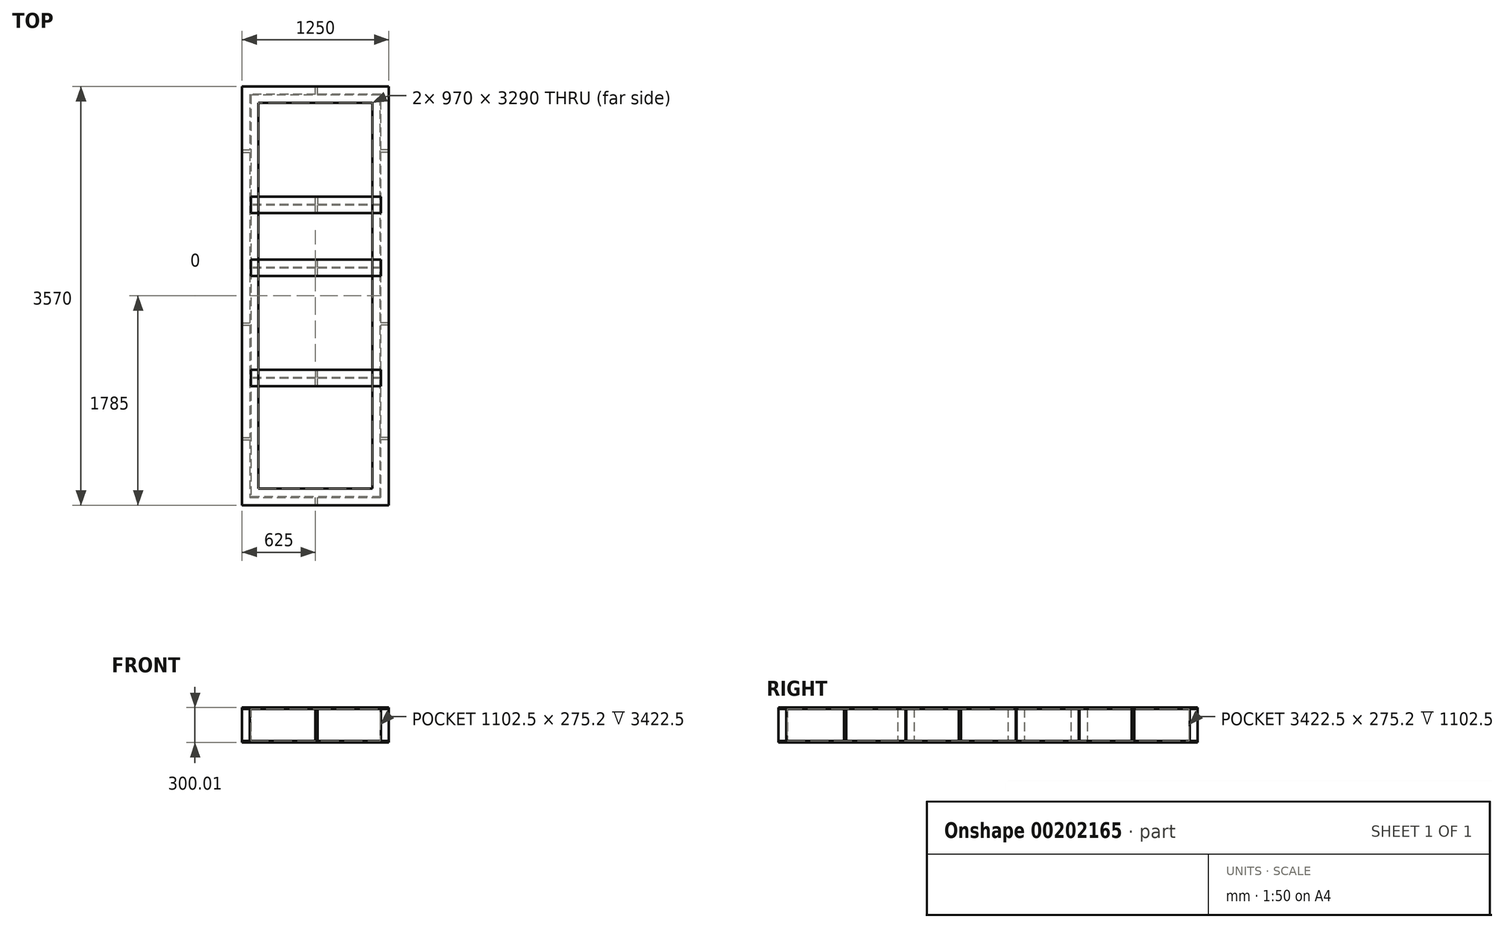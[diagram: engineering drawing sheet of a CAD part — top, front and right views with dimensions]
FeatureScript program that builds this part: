
annotation { "Feature Type Name" : "Feature", "Feature Type Description" : "" }
export const myFeature = defineFeature(function(context is Context, id is Id, definition is map)
    precondition{}
    {
        {
            var Q0;
            Q0=qCreatedBy(makeId("Front.planeOp"),FACE);
            var sketch = newSketch(context, id + "F0", { "sketchPlane" : qUnion([Q0])});
            skLineSegment(sketch, "E0", {"start": v(0, 0) * mm, "end": v(0, -300) * mm, "construction": true});
            skLineSegment(sketch, "E1", {"start": v(0, 0) * mm, "end": v(70, 0) * mm});
            skLineSegment(sketch, "E2", {"start": v(0, 0) * mm, "end": v(-70, 0) * mm});
            skLineSegment(sketch, "E3", {"start": v(-70, 0) * mm, "end": v(-70, -12.4) * mm});
            skLineSegment(sketch, "E4", {"start": v(-70, -12.4) * mm, "end": v(-3.75, -12.4) * mm});
            skLineSegment(sketch, "E5", {"start": v(-3.75, -12.4) * mm, "end": v(-3.75, -287.6) * mm});
            skLineSegment(sketch, "E6", {"start": v(-3.75, -287.6) * mm, "end": v(-70, -287.6) * mm});
            skLineSegment(sketch, "E7", {"start": v(-70, -287.6) * mm, "end": v(-70, -300) * mm});
            skLineSegment(sketch, "E8", {"start": v(-70, -300) * mm, "end": v(70, -300) * mm});
            skLineSegment(sketch, "E9", {"start": v(70, -300) * mm, "end": v(70, -287.6) * mm});
            skLineSegment(sketch, "E10", {"start": v(70, -287.6) * mm, "end": v(3.75, -287.6) * mm});
            skLineSegment(sketch, "E11", {"start": v(3.75, -287.6) * mm, "end": v(3.75, -12.4) * mm});
            skLineSegment(sketch, "E12", {"start": v(3.75, -12.4) * mm, "end": v(70, -12.4) * mm});
            skLineSegment(sketch, "E13", {"start": v(70, -12.4) * mm, "end": v(70, 0) * mm});
            skSolve(sketch);
        }
        {
            var Q0;
            Q0=qCreatedBy(makeId("Right.planeOp"),FACE);
            var sketch = newSketch(context, id + "F1", { "sketchPlane" : qUnion([Q0])});
            skLineSegment(sketch, "E14", {"start": v(0, 0) * mm, "end": v(0, -150) * mm, "construction": true});
            skLineSegment(sketch, "E15", {"start": v(0, -150) * mm, "end": v(-3430, -150) * mm});
            skSolve(sketch);
        }
        {
            var Q0;
            Q0=qCreatedBy(makeId("Front.planeOp"),FACE);
            cPlane(context, id + "F2", {"entities" : qUnion([Q0]), "cplaneType" : CPlaneType.OFFSET, "offset" : 3430 * mm, "width" : 150 * mm, "height" : 150 * mm});
        }
        {
            var Q0;
            Q0=qCreatedBy(id+"F2.planeOp",FACE);
            var sketch = newSketch(context, id + "F3", { "sketchPlane" : qUnion([Q0])});
            skLineSegment(sketch, "E16", {"start": v(0, 0) * mm, "end": v(0, -150) * mm, "construction": true});
            skLineSegment(sketch, "E17", {"start": v(0, -150) * mm, "end": v(1110, -150) * mm});
            skSolve(sketch);
        }
        {
            var Q0;
            Q0=qCreatedBy(makeId("Right.planeOp"),FACE);
            cPlane(context, id + "F4", {"entities" : qUnion([Q0]), "cplaneType" : CPlaneType.OFFSET, "offset" : 1110 * mm, "width" : 150 * mm, "height" : 150 * mm});
        }
        {
            var Q0;
            Q0=qCreatedBy(id+"F4.planeOp",FACE);
            var sketch = newSketch(context, id + "F5", { "sketchPlane" : qUnion([Q0])});
            skLineSegment(sketch, "E18", {"start": v(0, 0) * mm, "end": v(0, -150) * mm, "construction": true});
            skLineSegment(sketch, "E19", {"start": v(0, -150) * mm, "end": v(-3430, -150) * mm});
            skSolve(sketch);
        }
        {
            var Q0;
            Q0=qCreatedBy(makeId("Front.planeOp"),FACE);
            var sketch = newSketch(context, id + "F6", { "sketchPlane" : qUnion([Q0])});
            skLineSegment(sketch, "E20", {"start": v(0, 0) * mm, "end": v(0, -150) * mm, "construction": true});
            skLineSegment(sketch, "E21", {"start": v(0, -150) * mm, "end": v(1110, -150) * mm});
            skSolve(sketch);
        }
        {
            var Q0;
            Q0=makeQuery(id+"F0.imprint","IMPRINT",FACE,{"disambiguationData":[TD([[makeQuery(id+"F0.imprint","IMPRINT",EDGE,{"derivedFrom":sQuery(id+"F0.wireOp",EDGE,"E1")}),-1.0]])]});
            var Q1;
            Q1=qConstructionFilter(qBodyType(qCreatedBy(id+"F0",EDGE),BodyType.WIRE),ConstructionObject.NO);
            var Q2;
            Q2=sQuery(id+"F1.wireOp",EDGE,"E15");
            var Q3;
            Q3=sQuery(id+"F3.wireOp",EDGE,"E17");
            var Q4;
            Q4=sQuery(id+"F5.wireOp",EDGE,"E19");
            var Q5;
            Q5=sQuery(id+"F6.wireOp",EDGE,"E21");
            sweep(context, id + "F7", {"profiles" : qUnion([Q0]), "surfaceProfiles" : qUnion([Q1]), "path" : qUnion([Q2, Q3, Q4, Q5])});
        }
        {
            var Q0;
            Q0=qCreatedBy(makeId("Front.planeOp"),FACE);
            cPlane(context, id + "F8", {"entities" : qUnion([Q0]), "cplaneType" : CPlaneType.OFFSET, "offset" : 940 * mm, "width" : 150 * mm, "height" : 150 * mm});
        }
        {
            var Q0;
            Q0=qCreatedBy(makeId("Front.planeOp"),FACE);
            cPlane(context, id + "F9", {"entities" : qUnion([Q0]), "cplaneType" : CPlaneType.OFFSET, "offset" : 1475 * mm, "width" : 150 * mm, "height" : 150 * mm});
        }
        {
            var Q0;
            Q0=qCreatedBy(makeId("Front.planeOp"),FACE);
            cPlane(context, id + "F10", {"entities" : qUnion([Q0]), "cplaneType" : CPlaneType.OFFSET, "offset" : 2415 * mm, "width" : 150 * mm, "height" : 150 * mm});
        }
        {
            var Q0;
            Q0=qCreatedBy(id+"F8.planeOp",FACE);
            var sketch = newSketch(context, id + "F11", { "sketchPlane" : qUnion([Q0])});
            skLineSegment(sketch, "E22", {"start": v(0, 0) * mm, "end": v(0, -150) * mm, "construction": true});
            skLineSegment(sketch, "E23", {"start": v(0, -150) * mm, "end": v(1110, -150) * mm});
            skSolve(sketch);
        }
        {
            var Q0;
            Q0=makeQuery(id+"F7.opSweep","SWEPT_FACE",FACE,{"disambiguationData":[OSD([sQuery(id+"F0.wireOp",EDGE,"E5"),sQuery(id+"F5.wireOp",EDGE,"E19")])]});
            var sketch = newSketch(context, id + "F12", { "sketchPlane" : qUnion([Q0])});
            skLineSegment(sketch, "E24", {"start": v(0, 0) * mm, "end": v(-940, 0) * mm, "construction": true});
            skLineSegment(sketch, "E25", {"start": v(-940, 0) * mm, "end": v(-940, -150) * mm, "construction": true});
            skLineSegment(sketch, "E26", {"start": v(-939.82, 0) * mm, "end": v(-939.82, -300) * mm, "construction": true});
            skLineSegment(sketch, "E27", {"start": v(-939.82, 0) * mm, "end": v(-869.82, 0) * mm});
            skLineSegment(sketch, "E28", {"start": v(-939.82, 0) * mm, "end": v(-1009.82, 0) * mm});
            skLineSegment(sketch, "E29", {"start": v(-1009.82, 0) * mm, "end": v(-1009.82, -12.4) * mm});
            skLineSegment(sketch, "E30", {"start": v(-1009.82, -12.4) * mm, "end": v(-943.57, -12.4) * mm});
            skLineSegment(sketch, "E31", {"start": v(-943.57, -12.4) * mm, "end": v(-943.57, -287.6) * mm});
            skLineSegment(sketch, "E32", {"start": v(-943.57, -287.6) * mm, "end": v(-1009.82, -287.6) * mm});
            skLineSegment(sketch, "E33", {"start": v(-1009.82, -287.6) * mm, "end": v(-1009.82, -300) * mm});
            skLineSegment(sketch, "E34", {"start": v(-1009.82, -300) * mm, "end": v(-869.82, -300) * mm});
            skLineSegment(sketch, "E35", {"start": v(-869.82, -300) * mm, "end": v(-869.82, -287.6) * mm});
            skLineSegment(sketch, "E36", {"start": v(-869.82, -287.6) * mm, "end": v(-936.07, -287.6) * mm});
            skLineSegment(sketch, "E37", {"start": v(-936.07, -287.6) * mm, "end": v(-936.07, -12.4) * mm});
            skLineSegment(sketch, "E38", {"start": v(-936.07, -12.4) * mm, "end": v(-869.82, -12.4) * mm});
            skLineSegment(sketch, "E39", {"start": v(-869.82, -12.4) * mm, "end": v(-869.82, 0) * mm});
            skSolve(sketch);
        }
        {
            var Q0;
            Q0=qSketchRegion(id+"F12",true);
            var Q1;
            Q1=sQuery(id+"F11.wireOp",EDGE,"E23");
            sweep(context, id + "F13", {"profiles" : qUnion([Q0]), "path" : qUnion([Q1])});
        }
        {
            var Q0;
            Q0=qCreatedBy(id+"F9.planeOp",FACE);
            var sketch = newSketch(context, id + "F14", { "sketchPlane" : qUnion([Q0])});
            skLineSegment(sketch, "E40", {"start": v(0, 0) * mm, "end": v(0, -150) * mm, "construction": true});
            skLineSegment(sketch, "E41", {"start": v(0, -150) * mm, "end": v(1110, -150) * mm});
            skSolve(sketch);
        }
        {
            var Q0;
            Q0=qCreatedBy(id+"F10.planeOp",FACE);
            var sketch = newSketch(context, id + "F15", { "sketchPlane" : qUnion([Q0])});
            skLineSegment(sketch, "E42", {"start": v(0, 0) * mm, "end": v(0, -150) * mm, "construction": true});
            skLineSegment(sketch, "E43", {"start": v(0, -150) * mm, "end": v(1110, -150) * mm});
            skSolve(sketch);
        }
        {
            var Q0;
            Q0=makeQuery(id+"F7.opSweep","SWEPT_FACE",FACE,{"disambiguationData":[OSD([sQuery(id+"F0.wireOp",EDGE,"E5"),sQuery(id+"F5.wireOp",EDGE,"E19")])]});
            var sketch = newSketch(context, id + "F16", { "sketchPlane" : qUnion([Q0])});
            skLineSegment(sketch, "E44", {"start": v(0, 0) * mm, "end": v(-2415, 0) * mm, "construction": true});
            skLineSegment(sketch, "E45", {"start": v(-2415, 0) * mm, "end": v(-2415, -150) * mm, "construction": true});
            skLineSegment(sketch, "E46", {"start": v(-2415.04, 0) * mm, "end": v(-2415.04, -300) * mm, "construction": true});
            skLineSegment(sketch, "E47", {"start": v(-2415.04, 0) * mm, "end": v(-2345.04, 0) * mm});
            skLineSegment(sketch, "E48", {"start": v(-2415.04, 0) * mm, "end": v(-2485.04, 0) * mm});
            skLineSegment(sketch, "E49", {"start": v(-2485.04, 0) * mm, "end": v(-2485.04, -12.4) * mm});
            skLineSegment(sketch, "E50", {"start": v(-2485.04, -12.4) * mm, "end": v(-2418.79, -12.4) * mm});
            skLineSegment(sketch, "E51", {"start": v(-2418.79, -12.4) * mm, "end": v(-2418.79, -287.6) * mm});
            skLineSegment(sketch, "E52", {"start": v(-2418.79, -287.6) * mm, "end": v(-2485.04, -287.6) * mm});
            skLineSegment(sketch, "E53", {"start": v(-2485.04, -287.6) * mm, "end": v(-2485.04, -300) * mm});
            skLineSegment(sketch, "E54", {"start": v(-2485.04, -300) * mm, "end": v(-2345.04, -300) * mm});
            skLineSegment(sketch, "E55", {"start": v(-2345.04, -300) * mm, "end": v(-2345.04, -287.6) * mm});
            skLineSegment(sketch, "E56", {"start": v(-2345.04, -287.6) * mm, "end": v(-2411.29, -287.6) * mm});
            skLineSegment(sketch, "E57", {"start": v(-2411.29, -287.6) * mm, "end": v(-2411.29, -12.4) * mm});
            skLineSegment(sketch, "E58", {"start": v(-2411.29, -12.4) * mm, "end": v(-2345.04, -12.4) * mm});
            skLineSegment(sketch, "E59", {"start": v(-2345.04, -12.4) * mm, "end": v(-2345.04, 0) * mm});
            skSolve(sketch);
        }
        {
            var Q0;
            {var subQ2=sQuery(id+"F16.wireOp",EDGE,"E56");Q0=makeQuery(id+"F16.imprint","IMPRINT",FACE,{"disambiguationData":[TD([[makeQuery(id+"F16.imprint","IMPRINT",EDGE,{"derivedFrom":subQ2}),-1.0]])]});}
            var sketch = newSketch(context, id + "F17", { "sketchPlane" : qUnion([Q0])});
            skLineSegment(sketch, "E60", {"start": v(0, 0) * mm, "end": v(-1475, 0) * mm, "construction": true});
            skLineSegment(sketch, "E61", {"start": v(-1475, 0) * mm, "end": v(-1475, -150) * mm, "construction": true});
            skLineSegment(sketch, "E62", {"start": v(-1474.96, 0) * mm, "end": v(-1474.96, -300) * mm, "construction": true});
            skLineSegment(sketch, "E63", {"start": v(-1474.96, 0) * mm, "end": v(-1404.96, 0) * mm});
            skLineSegment(sketch, "E64", {"start": v(-1474.96, 0) * mm, "end": v(-1544.96, 0) * mm});
            skLineSegment(sketch, "E65", {"start": v(-1544.96, 0) * mm, "end": v(-1544.96, -12.4) * mm});
            skLineSegment(sketch, "E66", {"start": v(-1544.96, -12.4) * mm, "end": v(-1478.7, -12.4) * mm});
            skLineSegment(sketch, "E67", {"start": v(-1478.7, -12.4) * mm, "end": v(-1478.7, -287.6) * mm});
            skLineSegment(sketch, "E68", {"start": v(-1478.7, -287.6) * mm, "end": v(-1544.96, -287.6) * mm});
            skLineSegment(sketch, "E69", {"start": v(-1544.96, -287.6) * mm, "end": v(-1544.96, -300) * mm});
            skLineSegment(sketch, "E70", {"start": v(-1544.96, -300) * mm, "end": v(-1404.96, -300) * mm});
            skLineSegment(sketch, "E71", {"start": v(-1404.96, -300) * mm, "end": v(-1404.96, -287.6) * mm});
            skLineSegment(sketch, "E72", {"start": v(-1404.96, -287.6) * mm, "end": v(-1471.2, -287.6) * mm});
            skLineSegment(sketch, "E73", {"start": v(-1471.2, -287.6) * mm, "end": v(-1471.2, -12.4) * mm});
            skLineSegment(sketch, "E74", {"start": v(-1471.2, -12.4) * mm, "end": v(-1404.96, -12.4) * mm});
            skLineSegment(sketch, "E75", {"start": v(-1404.96, -12.4) * mm, "end": v(-1404.96, 0) * mm});
            skSolve(sketch);
        }
        {
            var Q0;
            Q0=qSketchRegion(id+"F17",true);
            var Q1;
            Q1=sQuery(id+"F14.wireOp",EDGE,"E41");
            sweep(context, id + "F18", {"profiles" : qUnion([Q0]), "path" : qUnion([Q1])});
        }
        {
            var Q0;
            Q0=qSketchRegion(id+"F16",true);
            var Q1;
            Q1=sQuery(id+"F15.wireOp",EDGE,"E43");
            sweep(context, id + "F19", {"profiles" : qUnion([Q0]), "path" : qUnion([Q1])});
        }
        {
            var Q0;
            Q0=qCreatedBy(id+"F10.planeOp",FACE);
            cPlane(context, id + "F20", {"entities" : qUnion([Q0]), "cplaneType" : CPlaneType.OFFSET, "offset" : 470 * mm, "oppositeDirection" : true, "width" : 150 * mm, "height" : 150 * mm});
        }
        {
            var Q0;
            Q0=qCreatedBy(id+"F20.planeOp",FACE);
            var sketch = newSketch(context, id + "F21", { "sketchPlane" : qUnion([Q0])});
            skLineSegment(sketch, "E76.0", {"start": v(-70, -12.4) * mm, "end": v(0, -12.4) * mm});
            skLineSegment(sketch, "E77", {"start": v(-70, -12.4) * mm, "end": v(-70, -287.6) * mm});
            skLineSegment(sketch, "E78", {"start": v(-70, -287.6) * mm, "end": v(0, -287.6) * mm});
            skLineSegment(sketch, "E79", {"start": v(0, -287.6) * mm, "end": v(0, -12.4) * mm});
            skPoint(sketch, "E80.orphan", {"position": v(1180, -12.4) * mm});
            skSolve(sketch);
        }
        {
            var Q0;
            Q0=qSketchRegion(id+"F21",true);
            extrude(context, id + "F22", {"entities" : qUnion([Q0]), "operationType" : NewBodyOperationType.ADD, "depth" : 20 * mm});
        }
        {
            var Q0;
            Q0=makeQuery(id+"Fla3xzbbfieMJ2c_5.opBoolean","MERGE",FACE,{"derivedFrom":[makeQuery(id+"F7.opSweep","SWEPT_FACE",FACE,{"disambiguationData":[OSD([sQuery(id+"F0.wireOp",EDGE,"E5"),sQuery(id+"F5.wireOp",EDGE,"E19")])]}),makeQuery(id+"F13.opSweep","CAP_FACE",FACE,{"disambiguationData":[OSD([sQuery(id+"F11.wireOp",VERTEX,"E23.end"),sQuery(id+"F12.wireOp",EDGE,"E27"),sQuery(id+"F12.wireOp",EDGE,"E28"),sQuery(id+"F12.wireOp",EDGE,"E29"),sQuery(id+"F12.wireOp",EDGE,"E30"),sQuery(id+"F12.wireOp",EDGE,"E31"),sQuery(id+"F12.wireOp",EDGE,"E32"),sQuery(id+"F12.wireOp",EDGE,"E33"),sQuery(id+"F12.wireOp",EDGE,"E34"),sQuery(id+"F12.wireOp",EDGE,"E35"),sQuery(id+"F12.wireOp",EDGE,"E36"),sQuery(id+"F12.wireOp",EDGE,"E37"),sQuery(id+"F12.wireOp",EDGE,"E38"),sQuery(id+"F12.wireOp",EDGE,"E39")])],"isStart":true}),makeQuery(id+"F18.opSweep","CAP_FACE",FACE,{"disambiguationData":[OSD([sQuery(id+"F14.wireOp",VERTEX,"E41.end"),sQuery(id+"F17.wireOp",EDGE,"E63"),sQuery(id+"F17.wireOp",EDGE,"E64"),sQuery(id+"F17.wireOp",EDGE,"E65"),sQuery(id+"F17.wireOp",EDGE,"E66"),sQuery(id+"F17.wireOp",EDGE,"E67"),sQuery(id+"F17.wireOp",EDGE,"E68"),sQuery(id+"F17.wireOp",EDGE,"E69"),sQuery(id+"F17.wireOp",EDGE,"E70"),sQuery(id+"F17.wireOp",EDGE,"E71"),sQuery(id+"F17.wireOp",EDGE,"E72"),sQuery(id+"F17.wireOp",EDGE,"E73"),sQuery(id+"F17.wireOp",EDGE,"E74"),sQuery(id+"F17.wireOp",EDGE,"E75")])],"isStart":true}),makeQuery(id+"F19.opSweep","CAP_FACE",FACE,{"disambiguationData":[OSD([sQuery(id+"F15.wireOp",VERTEX,"E43.end"),sQuery(id+"F16.wireOp",EDGE,"E47"),sQuery(id+"F16.wireOp",EDGE,"E48"),sQuery(id+"F16.wireOp",EDGE,"E49"),sQuery(id+"F16.wireOp",EDGE,"E50"),sQuery(id+"F16.wireOp",EDGE,"E51"),sQuery(id+"F16.wireOp",EDGE,"E52"),sQuery(id+"F16.wireOp",EDGE,"E53"),sQuery(id+"F16.wireOp",EDGE,"E54"),sQuery(id+"F16.wireOp",EDGE,"E55"),sQuery(id+"F16.wireOp",EDGE,"E56"),sQuery(id+"F16.wireOp",EDGE,"E57"),sQuery(id+"F16.wireOp",EDGE,"E58"),sQuery(id+"F16.wireOp",EDGE,"E59")])],"isStart":true})]});
            var sketch = newSketch(context, id + "F23", { "sketchPlane" : qUnion([Q0])});
            skLineSegment(sketch, "E81.0", {"start": v(-1945, -12.4) * mm, "end": v(-1945, -287.6) * mm});
            skLineSegment(sketch, "E82.0", {"start": v(-1965, -12.4) * mm, "end": v(-1965, -287.6) * mm});
            skLineSegment(sketch, "E83", {"start": v(-1965, -12.4) * mm, "end": v(-1945, -12.4) * mm});
            skLineSegment(sketch, "E84", {"start": v(-1965, -287.6) * mm, "end": v(-1945, -287.6) * mm});
            skSolve(sketch);
        }
        {
            var Q0;
            Q0=qSketchRegion(id+"F23",true);
            extrude(context, id + "F24", {"entities" : qUnion([Q0]), "operationType" : NewBodyOperationType.ADD, "depth" : 66 * mm});
        }
        {
            var Q0;
            Q0=qCreatedBy(id+"F10.planeOp",FACE);
            cPlane(context, id + "F25", {"entities" : qUnion([Q0]), "cplaneType" : CPlaneType.OFFSET, "offset" : 507.5 * mm, "width" : 150 * mm, "height" : 150 * mm});
        }
        {
            var Q0;
            Q0=qCreatedBy(makeId("Front.planeOp"),FACE);
            cPlane(context, id + "F26", {"entities" : qUnion([Q0]), "cplaneType" : CPlaneType.OFFSET, "offset" : 470 * mm, "width" : 150 * mm, "height" : 150 * mm});
        }
        {
            var Q0;
            Q0=qCreatedBy(id+"F26.planeOp",FACE);
            var sketch = newSketch(context, id + "F27", { "sketchPlane" : qUnion([Q0])});
            skLineSegment(sketch, "E85.0", {"start": v(-70, -12.4) * mm, "end": v(0, -12.4) * mm});
            skLineSegment(sketch, "E86", {"start": v(-70, -12.4) * mm, "end": v(-70, -287.6) * mm});
            skLineSegment(sketch, "E87", {"start": v(-70, -287.6) * mm, "end": v(0, -287.6) * mm});
            skLineSegment(sketch, "E88", {"start": v(0, -287.6) * mm, "end": v(0, -12.4) * mm});
            skPoint(sketch, "E89.orphan", {"position": v(1180, -12.4) * mm});
            skSolve(sketch);
        }
        {
            var Q0;
            Q0=qSketchRegion(id+"F27",true);
            extrude(context, id + "F28", {"entities" : qUnion([Q0]), "operationType" : NewBodyOperationType.ADD, "depth" : 20 * mm});
        }
        {
            var Q0;
            Q0=qCreatedBy(id+"F25.planeOp",FACE);
            var sketch = newSketch(context, id + "F29", { "sketchPlane" : qUnion([Q0])});
            skLineSegment(sketch, "E90.0", {"start": v(-70, -12.4) * mm, "end": v(0, -12.4) * mm});
            skLineSegment(sketch, "E91", {"start": v(-70, -12.4) * mm, "end": v(-70, -287.6) * mm});
            skLineSegment(sketch, "E92", {"start": v(-70, -287.6) * mm, "end": v(0, -287.6) * mm});
            skLineSegment(sketch, "E93", {"start": v(0, -287.6) * mm, "end": v(0, -12.4) * mm});
            skPoint(sketch, "E94.orphan", {"position": v(1180, -12.4) * mm});
            skSolve(sketch);
        }
        {
            var Q0;
            Q0=qSketchRegion(id+"F29",true);
            extrude(context, id + "F30", {"entities" : qUnion([Q0]), "operationType" : NewBodyOperationType.ADD, "depth" : 20 * mm});
        }
        {
            var Q0;
            {var subQ1=sQuery(id+"F0.wireOp",EDGE,"E5");Q0=makeQuery(id+"F24.boolean.opBoolean","SPLIT",FACE,{"disambiguationData":[TD([makeQuery(id+"F24.opExtrude","SWEPT_FACE",FACE,{"disambiguationData":[OSD([sQuery(id+"F23.wireOp",EDGE,"E81.0")])]})])],"derivedFrom":makeQuery(id+"Fla3xzbbfieMJ2c_5.opBoolean","MERGE",FACE,{"derivedFrom":[makeQuery(id+"F7.opSweep","SWEPT_FACE",FACE,{"disambiguationData":[OSD([subQ1,sQuery(id+"F5.wireOp",EDGE,"E19")])]}),makeQuery(id+"F13.opSweep","CAP_FACE",FACE,{"disambiguationData":[OSD([sQuery(id+"F11.wireOp",VERTEX,"E23.end"),sQuery(id+"F12.wireOp",EDGE,"E27"),sQuery(id+"F12.wireOp",EDGE,"E28"),sQuery(id+"F12.wireOp",EDGE,"E29"),sQuery(id+"F12.wireOp",EDGE,"E30"),sQuery(id+"F12.wireOp",EDGE,"E31"),sQuery(id+"F12.wireOp",EDGE,"E32"),sQuery(id+"F12.wireOp",EDGE,"E33"),sQuery(id+"F12.wireOp",EDGE,"E34"),sQuery(id+"F12.wireOp",EDGE,"E35"),sQuery(id+"F12.wireOp",EDGE,"E36"),sQuery(id+"F12.wireOp",EDGE,"E37"),sQuery(id+"F12.wireOp",EDGE,"E38"),sQuery(id+"F12.wireOp",EDGE,"E39")])],"isStart":true}),makeQuery(id+"F18.opSweep","CAP_FACE",FACE,{"disambiguationData":[OSD([sQuery(id+"F14.wireOp",VERTEX,"E41.end"),sQuery(id+"F17.wireOp",EDGE,"E63"),sQuery(id+"F17.wireOp",EDGE,"E64"),sQuery(id+"F17.wireOp",EDGE,"E65"),sQuery(id+"F17.wireOp",EDGE,"E66"),sQuery(id+"F17.wireOp",EDGE,"E67"),sQuery(id+"F17.wireOp",EDGE,"E68"),sQuery(id+"F17.wireOp",EDGE,"E69"),sQuery(id+"F17.wireOp",EDGE,"E70"),sQuery(id+"F17.wireOp",EDGE,"E71"),sQuery(id+"F17.wireOp",EDGE,"E72"),sQuery(id+"F17.wireOp",EDGE,"E73"),sQuery(id+"F17.wireOp",EDGE,"E74"),sQuery(id+"F17.wireOp",EDGE,"E75")])],"isStart":true}),makeQuery(id+"F19.opSweep","CAP_FACE",FACE,{"disambiguationData":[OSD([sQuery(id+"F15.wireOp",VERTEX,"E43.end"),sQuery(id+"F16.wireOp",EDGE,"E47"),sQuery(id+"F16.wireOp",EDGE,"E48"),sQuery(id+"F16.wireOp",EDGE,"E49"),sQuery(id+"F16.wireOp",EDGE,"E50"),sQuery(id+"F16.wireOp",EDGE,"E51"),sQuery(id+"F16.wireOp",EDGE,"E52"),sQuery(id+"F16.wireOp",EDGE,"E53"),sQuery(id+"F16.wireOp",EDGE,"E54"),sQuery(id+"F16.wireOp",EDGE,"E55"),sQuery(id+"F16.wireOp",EDGE,"E56"),sQuery(id+"F16.wireOp",EDGE,"E57"),sQuery(id+"F16.wireOp",EDGE,"E58"),sQuery(id+"F16.wireOp",EDGE,"E59")])],"isStart":true})]})});}
            var sketch = newSketch(context, id + "F31", { "sketchPlane" : qUnion([Q0])});
            skLineSegment(sketch, "E95.0", {"start": v(-470, -12.4) * mm, "end": v(-470, -287.6) * mm});
            skLineSegment(sketch, "E96.0", {"start": v(-490, -12.4) * mm, "end": v(-490, -287.6) * mm});
            skLineSegment(sketch, "E97.0", {"start": v(-2922.5, -12.4) * mm, "end": v(-2922.5, -287.6) * mm});
            skLineSegment(sketch, "E98.0", {"start": v(-2942.5, -12.4) * mm, "end": v(-2942.5, -287.6) * mm});
            skLineSegment(sketch, "E99", {"start": v(-2942.5, -12.4) * mm, "end": v(-2922.5, -12.4) * mm});
            skLineSegment(sketch, "E100", {"start": v(-2942.5, -287.6) * mm, "end": v(-2922.5, -287.6) * mm});
            skLineSegment(sketch, "E101", {"start": v(-490, -12.4) * mm, "end": v(-470, -12.4) * mm});
            skLineSegment(sketch, "E102", {"start": v(-490, -287.6) * mm, "end": v(-470, -287.6) * mm});
            skSolve(sketch);
        }
        {
            var Q0;
            Q0=qSketchRegion(id+"F31",true);
            extrude(context, id + "F32", {"entities" : qUnion([Q0]), "operationType" : NewBodyOperationType.ADD, "depth" : 66 * mm});
        }
        {
            var Q0;
            Q0=qCreatedBy(makeId("Right.planeOp"),FACE);
            cPlane(context, id + "F33", {"entities" : qUnion([Q0]), "cplaneType" : CPlaneType.OFFSET, "offset" : 555 * mm, "width" : 150 * mm, "height" : 150 * mm});
        }
        {
            var Q0;
            Q0=qCreatedBy(id+"F33.planeOp",FACE);
            var sketch = newSketch(context, id + "F34", { "sketchPlane" : qUnion([Q0])});
            skLineSegment(sketch, "E103.0", {"start": v(0, -12.4) * mm, "end": v(70, -12.4) * mm});
            skLineSegment(sketch, "E104", {"start": v(70, -12.4) * mm, "end": v(70, -287.6) * mm});
            skLineSegment(sketch, "E105", {"start": v(70, -287.6) * mm, "end": v(0, -287.6) * mm});
            skLineSegment(sketch, "E106", {"start": v(0, -287.6) * mm, "end": v(0, -12.4) * mm});
            skPoint(sketch, "E107.orphan", {"position": v(-3500, -12.4) * mm});
            skSolve(sketch);
        }
        {
            var Q0;
            Q0=qSketchRegion(id+"F34",true);
            extrude(context, id + "F35", {"entities" : qUnion([Q0]), "operationType" : NewBodyOperationType.ADD, "depth" : 20 * mm});
        }
        {
            var Q0;
            Q0=makeQuery(id+"F7.opSweep","SWEPT_FACE",FACE,{"disambiguationData":[OSD([sQuery(id+"F0.wireOp",EDGE,"E5"),sQuery(id+"F3.wireOp",EDGE,"E17")])]});
            var sketch = newSketch(context, id + "F36", { "sketchPlane" : qUnion([Q0])});
            skLineSegment(sketch, "E108.0", {"start": v(575, -12.4) * mm, "end": v(575, -287.6) * mm});
            skLineSegment(sketch, "E109.0", {"start": v(555, -12.4) * mm, "end": v(555, -287.6) * mm});
            skLineSegment(sketch, "E110", {"start": v(555, -12.4) * mm, "end": v(575, -12.4) * mm});
            skLineSegment(sketch, "E111", {"start": v(555, -287.6) * mm, "end": v(575, -287.6) * mm});
            skSolve(sketch);
        }
        {
            var Q0;
            Q0=qSketchRegion(id+"F36",true);
            extrude(context, id + "F37", {"entities" : qUnion([Q0]), "operationType" : NewBodyOperationType.ADD, "depth" : 66 * mm});
        }
        {
            var Q0;
            Q0=makeQuery(id+"F19.opSweep","SWEPT_FACE",FACE,{"disambiguationData":[OSD([sQuery(id+"F15.wireOp",EDGE,"E43"),sQuery(id+"F16.wireOp",EDGE,"E51")])]});
            var sketch = newSketch(context, id + "F38", { "sketchPlane" : qUnion([Q0])});
            skLineSegment(sketch, "E112.0", {"start": v(555, -12.4) * mm, "end": v(555, -287.6) * mm});
            skLineSegment(sketch, "E113.0", {"start": v(575, -12.4) * mm, "end": v(575, -287.6) * mm});
            skLineSegment(sketch, "E114", {"start": v(555, -12.4) * mm, "end": v(575, -12.4) * mm});
            skLineSegment(sketch, "E115", {"start": v(555, -287.6) * mm, "end": v(575, -287.6) * mm});
            skSolve(sketch);
        }
        {
            var Q0;
            Q0=qSketchRegion(id+"F38",true);
            extrude(context, id + "F39", {"entities" : qUnion([Q0]), "operationType" : NewBodyOperationType.ADD, "depth" : 66 * mm});
        }
        {
            var Q0;
            Q0=makeQuery(id+"F19.opSweep","SWEPT_FACE",FACE,{"disambiguationData":[OSD([sQuery(id+"F15.wireOp",EDGE,"E43"),sQuery(id+"F16.wireOp",EDGE,"E57")])]});
            var sketch = newSketch(context, id + "F40", { "sketchPlane" : qUnion([Q0])});
            skLineSegment(sketch, "E116.0", {"start": v(-555, -12.4) * mm, "end": v(-555, -287.6) * mm});
            skLineSegment(sketch, "E117.0", {"start": v(-575, -12.4) * mm, "end": v(-575, -287.6) * mm});
            skLineSegment(sketch, "E118", {"start": v(-555, -12.4) * mm, "end": v(-575, -12.4) * mm});
            skLineSegment(sketch, "E119", {"start": v(-555, -287.6) * mm, "end": v(-575, -287.6) * mm});
            skSolve(sketch);
        }
        {
            var Q0;
            Q0=qSketchRegion(id+"F40",true);
            extrude(context, id + "F41", {"entities" : qUnion([Q0]), "operationType" : NewBodyOperationType.ADD, "depth" : 66 * mm});
        }
        {
            var Q0;
            Q0=makeQuery(id+"F18.opSweep","SWEPT_FACE",FACE,{"disambiguationData":[OSD([sQuery(id+"F14.wireOp",EDGE,"E41"),sQuery(id+"F17.wireOp",EDGE,"E67")])]});
            var sketch = newSketch(context, id + "F42", { "sketchPlane" : qUnion([Q0])});
            skLineSegment(sketch, "E120.0", {"start": v(555, -12.4) * mm, "end": v(555, -287.6) * mm});
            skLineSegment(sketch, "E121.0", {"start": v(575, -12.4) * mm, "end": v(575, -287.6) * mm});
            skLineSegment(sketch, "E122", {"start": v(555, -12.4) * mm, "end": v(575, -12.4) * mm});
            skLineSegment(sketch, "E123", {"start": v(555, -287.6) * mm, "end": v(575, -287.6) * mm});
            skSolve(sketch);
        }
        {
            var Q0;
            Q0=qSketchRegion(id+"F42",true);
            extrude(context, id + "F43", {"entities" : qUnion([Q0]), "operationType" : NewBodyOperationType.ADD, "depth" : 66 * mm});
        }
        {
            var Q0;
            Q0=makeQuery(id+"F18.opSweep","SWEPT_FACE",FACE,{"disambiguationData":[OSD([sQuery(id+"F14.wireOp",EDGE,"E41"),sQuery(id+"F17.wireOp",EDGE,"E73")])]});
            var sketch = newSketch(context, id + "F44", { "sketchPlane" : qUnion([Q0])});
            skLineSegment(sketch, "E124.0", {"start": v(-575, -12.4) * mm, "end": v(-575, -287.6) * mm});
            skLineSegment(sketch, "E125.0", {"start": v(-555, -12.4) * mm, "end": v(-555, -287.6) * mm});
            skLineSegment(sketch, "E126", {"start": v(-575, -12.4) * mm, "end": v(-555, -12.4) * mm});
            skLineSegment(sketch, "E127", {"start": v(-575, -287.6) * mm, "end": v(-555, -287.6) * mm});
            skSolve(sketch);
        }
        {
            var Q0;
            Q0=qSketchRegion(id+"F44",true);
            extrude(context, id + "F45", {"entities" : qUnion([Q0]), "operationType" : NewBodyOperationType.ADD, "depth" : 66 * mm});
        }
        {
            var Q0;
            Q0=makeQuery(id+"F13.opSweep","SWEPT_FACE",FACE,{"disambiguationData":[OSD([sQuery(id+"F11.wireOp",EDGE,"E23"),sQuery(id+"F12.wireOp",EDGE,"E37")])]});
            var sketch = newSketch(context, id + "F46", { "sketchPlane" : qUnion([Q0])});
            skLineSegment(sketch, "E128.0", {"start": v(-575, -12.4) * mm, "end": v(-575, -287.6) * mm});
            skLineSegment(sketch, "E129.0", {"start": v(-555, -12.4) * mm, "end": v(-555, -287.6) * mm});
            skLineSegment(sketch, "E130", {"start": v(-575, -12.4) * mm, "end": v(-555, -12.4) * mm});
            skLineSegment(sketch, "E131", {"start": v(-575, -287.6) * mm, "end": v(-555, -287.6) * mm});
            skSolve(sketch);
        }
        {
            var Q0;
            Q0=qSketchRegion(id+"F46",true);
            extrude(context, id + "F47", {"entities" : qUnion([Q0]), "operationType" : NewBodyOperationType.ADD, "depth" : 66 * mm});
        }
        {
            var Q0;
            Q0=makeQuery(id+"F13.opSweep","SWEPT_FACE",FACE,{"disambiguationData":[OSD([sQuery(id+"F11.wireOp",EDGE,"E23"),sQuery(id+"F12.wireOp",EDGE,"E31")])]});
            var sketch = newSketch(context, id + "F48", { "sketchPlane" : qUnion([Q0])});
            skLineSegment(sketch, "E132.0", {"start": v(555, -12.4) * mm, "end": v(555, -287.6) * mm});
            skLineSegment(sketch, "E133.0", {"start": v(575, -12.4) * mm, "end": v(575, -287.6) * mm});
            skLineSegment(sketch, "E134", {"start": v(555, -12.4) * mm, "end": v(575, -12.4) * mm});
            skLineSegment(sketch, "E135", {"start": v(555, -287.6) * mm, "end": v(575, -287.6) * mm});
            skSolve(sketch);
        }
        {
            var Q0;
            Q0=qSketchRegion(id+"F48",true);
            extrude(context, id + "F49", {"entities" : qUnion([Q0]), "operationType" : NewBodyOperationType.ADD, "depth" : 66 * mm});
        }
    });
